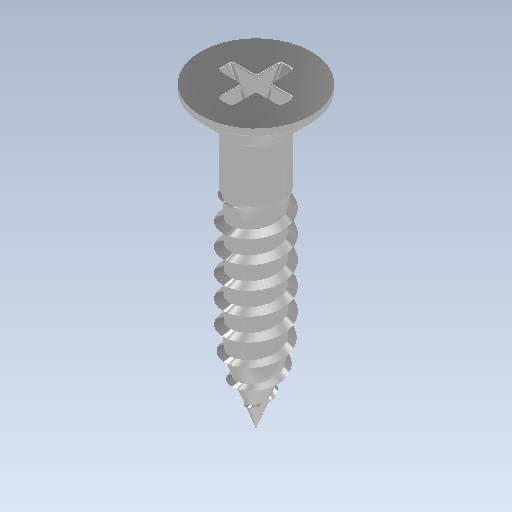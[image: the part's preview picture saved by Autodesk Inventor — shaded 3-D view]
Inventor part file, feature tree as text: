
AUTODESK INVENTOR PART (.ipt)
format: ipt  version: 2021 (Build 250183000, 183)  size: 457,728 bytes
history: native  units: mm (DEFAULTED — no unit token found)
features: sketch x9, helix x7, fillet x3, revolve x1, extrude x1, pattern_circular x1, projected_geometry x1
ambient origin geometry x8: Origin, YZ Plane, XZ Plane, XY Plane, X Axis, Y Axis, Z Axis, Center Point
bodies: Solid1 (feature_tree)
feature tree (23):
  revolve  "Revolution1"  [1 undecoded]
  helix  "Coil1"  [1 undecoded]
  helix  "Coil3"  [1 undecoded]
  helix  "Coil9"  [1 undecoded]
  helix  "Coil5"  [1 undecoded]
  helix  "Coil6"  [1 undecoded]
  helix  "Coil7"  [1 undecoded]
  helix  "Coil8"  [1 undecoded]
  extrude  "Extrusion1"  Depth=4.2mm
  pattern_circular  "Circular Pattern1"  [2 undecoded]
  fillet  "Fillet2"  Radius=0.1mm
  fillet  "Fillet1"  Radius=10.821041mm
  fillet  "Fillet3"  Radius=0.5mm
  sketch  "Sketch1"  dims[d0=4.2mm d1=2.0mm d2=45.0deg d3=27.925268mm d4=2.7mm d5=3.8mm d6=20.0mm d7=90.0deg d8=4.0mm]
  sketch  "Sketch2"  dims[d9=1.75mm d10=4.2mm]
  projected_geometry  "Projected Loop1"
  sketch  "Sketch4"  dims[d11=60.0deg]
  sketch  "Sketch7"  dims[d12=60.0deg]
  sketch  "Sketch8"  dims[d13=0.5mm]
  sketch  "Sketch9"  dims[d14=0.0mm]
  sketch  "Sketch10"  dims[d15=1.7mm d16=10.0mm d17=45.0mm d18=0.0mm d19=90.0deg d20=90.0deg d21=0.0mm d22=0.0mm]
  sketch  "Sketch11"  dims[d37=1.75mm d38=10.0mm d39=2.5mm d40=0.0mm d41=90.0deg d42=90.0deg d43=0.0mm d44=0.0mm]
  sketch  "Sketch12"  dims[d53=1.75mm d54=10.0mm d55=10.0mm d56=-0.872665mm d57=90.0deg d58=90.0deg d59=0.0mm d60=0.0mm d61=1.75mm d62=10.0mm d63=5.0mm d64=0.0mm d65=90.0deg d66=90.0deg d67=0.0mm d68=0.0mm d69=0.1mm d70=0.1mm d71=1.75mm d72=10.0mm d73=5.0mm d74=-1.745329mm d75=90.0deg d76=90.0deg d77=0.0mm d78=0.0mm d79=1.75mm d80=10.0mm d81=10.0mm d82=-5.235988mm d83=90.0deg d84=90.0deg d85=0.0mm d86=0.0mm d103=10.821041mm d135=0.5mm d136=0.5mm d137=0.0mm d138=0.0mm d139=40.0mm d140=360.0deg d142=0.2mm d143=0.2mm d144=0.8mm d146=3.0mm d147=1.75mm d148=10.0mm d149=7.5mm d150=-3.141593mm d151=90.0deg d152=90.0deg d153=0.0mm d154=0.0mm d155=0.1mm]
note: 10 required parameter values undecoded (feature->parameter linkage not recoverable at this tier; creation-order binding heuristic only, values carry confidence <= 0.55)